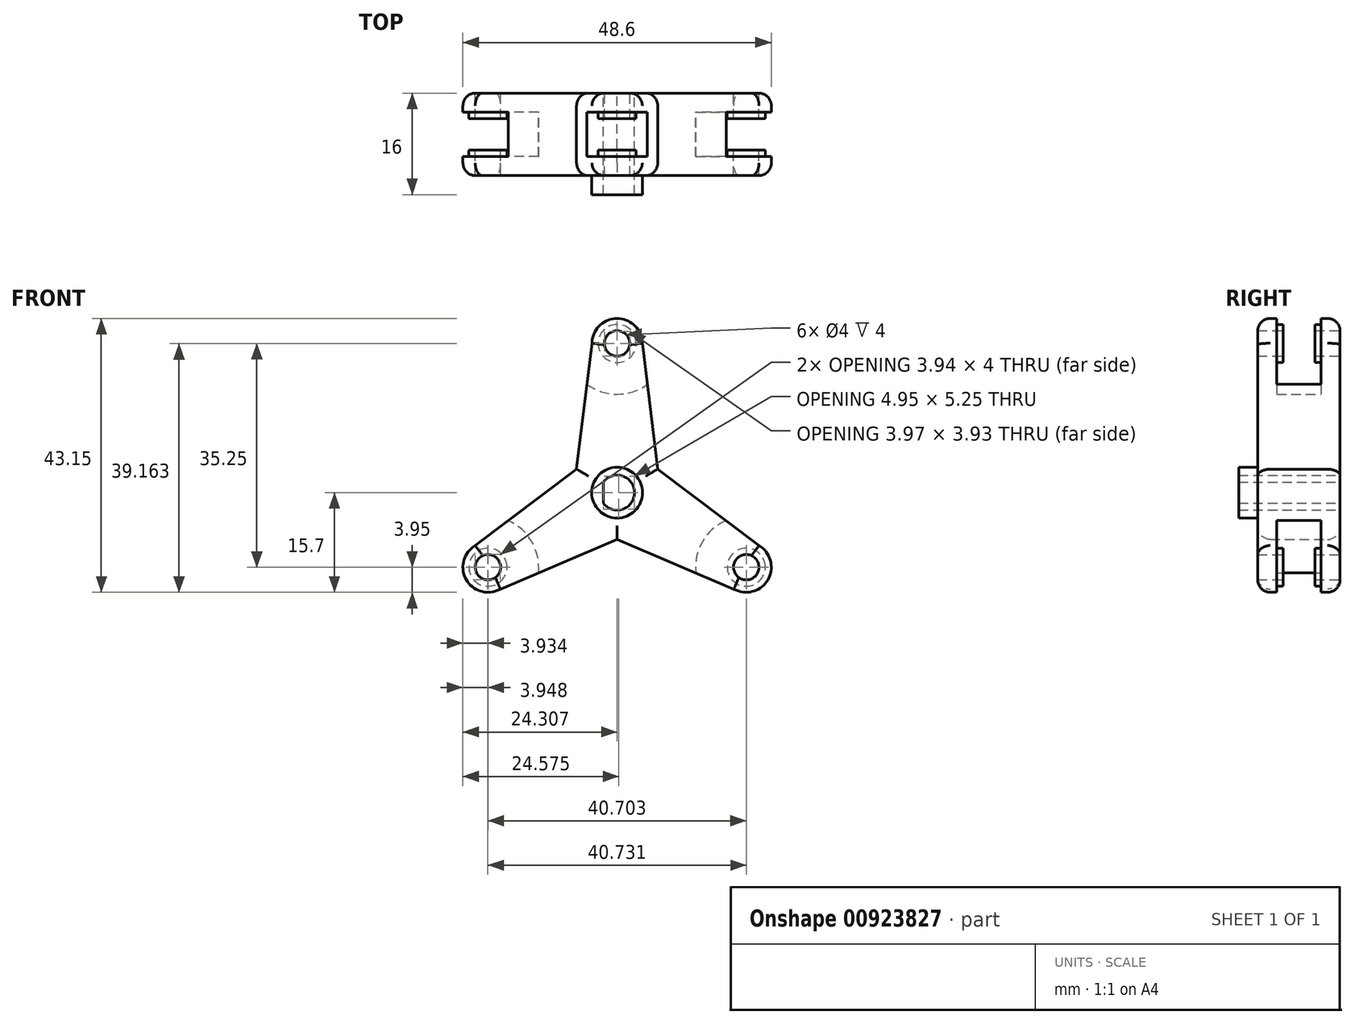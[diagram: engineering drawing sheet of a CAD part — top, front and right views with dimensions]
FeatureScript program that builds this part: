
annotation { "Feature Type Name" : "Feature", "Feature Type Description" : "" }
export const myFeature = defineFeature(function(context is Context, id is Id, definition is map)
    precondition{}
    {
        {
            var Q0;
            Q0=qCreatedBy(makeId("Front.planeOp"),FACE);
            var sketch = newSketch(context, id + "F0", { "sketchPlane" : qUnion([Q0])});
            skPoint(sketch, "E0", {"position": v(0, 23.5) * mm});
            skCircle(sketch, "E1", {"center": v(0, 23.5) * mm, "radius": 2 * mm});
            skPoint(sketch, "E2.center", {"position": v(0, 0) * mm});
            skArc(sketch, "E3", {"start": v(-2.2, -1.65) * mm, "mid": v(2.75, 0) * mm, "end": v(-2.2, 1.65) * mm});
            skCircle(sketch, "E4", {"center": v(0, 0) * mm, "radius": 4 * mm});
            skCircle(sketch, "E5", {"center": v(0, 23.5) * mm, "radius": 3 * mm});
            skArc(sketch, "E6", {"start": v(-4.76, 17.07) * mm, "mid": v(0, 15.5) * mm, "end": v(4.76, 17.07) * mm});
            skArc(sketch, "E7", {"start": v(3.92, 23.98) * mm, "mid": v(0, 27.45) * mm, "end": v(-3.92, 23.98) * mm});
            skLineSegment(sketch, "E8", {"start": v(-7.5, -5.33) * mm, "end": v(-3.92, 23.98) * mm});
            skLineSegment(sketch, "E9.MirrorCS", {"start": v(7.5, -5.33) * mm, "end": v(3.92, 23.98) * mm});
            skLineSegment(sketch, "E10", {"start": v(-2.2, 1.65) * mm, "end": v(-2.2, -1.65) * mm});
            skPoint(sketch, "E11.center", {"position": v(-0.14, 0.25) * mm});
            skArc(sketch, "E12.1.0", {"start": v(-22.73, -8.6) * mm, "mid": v(-23.77, -13.73) * mm, "end": v(-18.8, -15.39) * mm});
            skCircle(sketch, "E12.1.1", {"center": v(-20.35, -11.75) * mm, "radius": 2 * mm});
            skCircle(sketch, "E12.1.2", {"center": v(-20.35, -11.75) * mm, "radius": 3 * mm});
            skArc(sketch, "E12.1.3", {"start": v(-12.4, -12.66) * mm, "mid": v(-13.42, -7.75) * mm, "end": v(-17.17, -4.41) * mm});
            skPoint(sketch, "E12.1.4", {"position": v(-20.35, -11.75) * mm});
            skLineSegment(sketch, "E12.1.5", {"start": v(0.87, 9.16) * mm, "end": v(-22.73, -8.6) * mm});
            skLineSegment(sketch, "E12.1.6", {"start": v(8.37, -3.83) * mm, "end": v(-18.8, -15.39) * mm});
            skArc(sketch, "E12.2.0", {"start": v(18.8, -15.39) * mm, "mid": v(23.77, -13.73) * mm, "end": v(22.73, -8.6) * mm});
            skCircle(sketch, "E12.2.1", {"center": v(20.35, -11.75) * mm, "radius": 2 * mm});
            skCircle(sketch, "E12.2.2", {"center": v(20.35, -11.75) * mm, "radius": 3 * mm});
            skArc(sketch, "E12.2.3", {"start": v(17.17, -4.41) * mm, "mid": v(13.42, -7.75) * mm, "end": v(12.4, -12.66) * mm});
            skPoint(sketch, "E12.2.4", {"position": v(20.35, -11.75) * mm});
            skLineSegment(sketch, "E12.2.5", {"start": v(-8.37, -3.83) * mm, "end": v(18.8, -15.39) * mm});
            skLineSegment(sketch, "E12.2.6", {"start": v(-0.87, 9.16) * mm, "end": v(22.73, -8.6) * mm});
            skPoint(sketch, "E13", {"position": v(0, 27.45) * mm});
            skSolve(sketch);
        }
        {
            var Q0;
            Q0=makeQuery(id+"F0.imprint","IMPRINT",FACE,{"disambiguationData":[TD([[makeQuery(id+"F0.imprint","IMPRINT",EDGE,{"derivedFrom":sQuery(id+"F0.wireOp",EDGE,"E1")}),-1.0]])]});
            var Q1;
            Q1=makeQuery(id+"F0.imprint","IMPRINT",FACE,{"disambiguationData":[TD([[makeQuery(id+"F0.imprint","IMPRINT",EDGE,{"derivedFrom":sQuery(id+"F0.wireOp",EDGE,"E5")}),-1.0]])]});
            var Q2;
            {var subQ1=sQuery(id+"F0.wireOp",EDGE,"E6");Q2=makeQuery(id+"F0.imprint","IMPRINT",FACE,{"disambiguationData":[TD([[makeQuery(id+"F0.imprint","IMPRINT",EDGE,{"derivedFrom":subQ1}),-1.0]])]});}
            var Q3;
            {var subQ1=sQuery(id+"F0.wireOp",EDGE,"E12.2.3");Q3=makeQuery(id+"F0.imprint","IMPRINT",FACE,{"disambiguationData":[TD([[makeQuery(id+"F0.imprint","IMPRINT",EDGE,{"derivedFrom":subQ1}),-1.0]])]});}
            var Q4;
            {var subQ1=sQuery(id+"F0.wireOp",EDGE,"E12.2.0");Q4=makeQuery(id+"F0.imprint","IMPRINT",FACE,{"disambiguationData":[TD([[makeQuery(id+"F0.imprint","IMPRINT",EDGE,{"derivedFrom":subQ1}),1.0]])]});}
            var Q5;
            Q5=makeQuery(id+"F0.imprint","IMPRINT",FACE,{"disambiguationData":[TD([[makeQuery(id+"F0.imprint","IMPRINT",EDGE,{"derivedFrom":sQuery(id+"F0.wireOp",EDGE,"E12.2.1")}),-1.0]])]});
            var Q6;
            {var subQ1=sQuery(id+"F0.wireOp",EDGE,"E12.1.3");Q6=makeQuery(id+"F0.imprint","IMPRINT",FACE,{"disambiguationData":[TD([[makeQuery(id+"F0.imprint","IMPRINT",EDGE,{"derivedFrom":subQ1}),-1.0]])]});}
            var Q7;
            {var subQ1=sQuery(id+"F0.wireOp",EDGE,"E12.1.0");Q7=makeQuery(id+"F0.imprint","IMPRINT",FACE,{"disambiguationData":[TD([[makeQuery(id+"F0.imprint","IMPRINT",EDGE,{"derivedFrom":subQ1}),1.0]])]});}
            var Q8;
            Q8=makeQuery(id+"F0.imprint","IMPRINT",FACE,{"disambiguationData":[TD([[makeQuery(id+"F0.imprint","IMPRINT",EDGE,{"derivedFrom":sQuery(id+"F0.wireOp",EDGE,"E12.1.1")}),-1.0]])]});
            var Q9;
            Q9=makeQuery(id+"F0.imprint","IMPRINT",FACE,{"disambiguationData":[TD([[makeQuery(id+"F0.imprint","IMPRINT",EDGE,{"derivedFrom":sQuery(id+"F0.wireOp",EDGE,"E4")}),-1.0]])]});
            extrude(context, id + "F1", {"entities" : qUnion([Q0, Q1, Q2, Q3, Q4, Q5, Q6, Q7, Q8, Q9]), "depth" : 13 * mm, "offsetDistance" : 25 * mm});
        }
        {
            var Q0;
            Q0=makeQuery(id+"F0.imprint","IMPRINT",FACE,{"disambiguationData":[TD([[makeQuery(id+"F0.imprint","IMPRINT",EDGE,{"derivedFrom":sQuery(id+"F0.wireOp",EDGE,"E3")}),-1.0]])]});
            extrude(context, id + "F2", {"entities" : qUnion([Q0]), "operationType" : NewBodyOperationType.ADD, "depth" : 16 * mm, "offsetDistance" : 25 * mm});
        }
        {
            var Q0;
            Q0=makeQuery(id+"F0.imprint","IMPRINT",FACE,{"disambiguationData":[TD([[makeQuery(id+"F0.imprint","IMPRINT",EDGE,{"derivedFrom":sQuery(id+"F0.wireOp",EDGE,"E5")}),-1.0]])]});
            var Q1;
            {var subQ1=sQuery(id+"F0.wireOp",EDGE,"E12.1.0");Q1=makeQuery(id+"F0.imprint","IMPRINT",FACE,{"disambiguationData":[TD([[makeQuery(id+"F0.imprint","IMPRINT",EDGE,{"derivedFrom":subQ1}),1.0]])]});}
            var Q2;
            {var subQ1=sQuery(id+"F0.wireOp",EDGE,"E12.2.0");Q2=makeQuery(id+"F0.imprint","IMPRINT",FACE,{"disambiguationData":[TD([[makeQuery(id+"F0.imprint","IMPRINT",EDGE,{"derivedFrom":subQ1}),1.0]])]});}
            extrude(context, id + "F3", {"entities" : qUnion([Q0, Q1, Q2]), "operationType" : NewBodyOperationType.REMOVE, "endBound" : BoundingType.UP_TO_NEXT, "depth" : 25 * mm, "hasOffset" : true, "offsetDistance" : 3 * mm, "hasSecondDirection" : true, "secondDirectionOppositeDirection" : false, "secondDirectionDepth" : 3 * mm});
        }
        {
            var Q0;
            Q0=makeQuery(id+"F0.imprint","IMPRINT",FACE,{"disambiguationData":[TD([[makeQuery(id+"F0.imprint","IMPRINT",EDGE,{"derivedFrom":sQuery(id+"F0.wireOp",EDGE,"E1")}),-1.0]])]});
            var Q1;
            Q1=makeQuery(id+"F0.imprint","IMPRINT",FACE,{"disambiguationData":[TD([[makeQuery(id+"F0.imprint","IMPRINT",EDGE,{"derivedFrom":sQuery(id+"F0.wireOp",EDGE,"E12.1.1")}),-1.0]])]});
            var Q2;
            Q2=makeQuery(id+"F0.imprint","IMPRINT",FACE,{"disambiguationData":[TD([[makeQuery(id+"F0.imprint","IMPRINT",EDGE,{"derivedFrom":sQuery(id+"F0.wireOp",EDGE,"E12.2.1")}),-1.0]])]});
            extrude(context, id + "F4", {"entities" : qUnion([Q0, Q1, Q2]), "operationType" : NewBodyOperationType.REMOVE, "endBound" : BoundingType.UP_TO_NEXT, "depth" : 25 * mm, "hasOffset" : true, "offsetDistance" : 4 * mm, "hasSecondDirection" : true, "secondDirectionOppositeDirection" : false, "secondDirectionDepth" : 4 * mm});
        }
        {
            var Q0;
            Q0=makeQuery(id+"F1.opExtrude","CAP_EDGE",EDGE,{"disambiguationData":[OSD([sQuery(id+"F0.wireOp",EDGE,"E8")])],"isStart":false});
            var Q1;
            Q1=makeQuery(id+"F1.opExtrude","CAP_EDGE",EDGE,{"disambiguationData":[OSD([sQuery(id+"F0.wireOp",EDGE,"E12.2.6")])],"isStart":false});
            var Q2;
            Q2=makeQuery(id+"F1.opExtrude","CAP_EDGE",EDGE,{"disambiguationData":[OSD([sQuery(id+"F0.wireOp",EDGE,"E12.1.6")])],"isStart":false});
            var Q3;
            Q3=makeQuery(id+"F1.opExtrude","CAP_EDGE",EDGE,{"disambiguationData":[OSD([sQuery(id+"F0.wireOp",EDGE,"E9.MirrorCS")])],"isStart":true});
            var Q4;
            Q4=makeQuery(id+"F1.opExtrude","CAP_EDGE",EDGE,{"disambiguationData":[OSD([sQuery(id+"F0.wireOp",EDGE,"E12.1.5")])],"isStart":true});
            var Q5;
            Q5=makeQuery(id+"F1.opExtrude","CAP_EDGE",EDGE,{"disambiguationData":[OSD([sQuery(id+"F0.wireOp",EDGE,"E12.2.5")])],"isStart":true});
            var Q6;
            Q6=makeQuery(id+"F3.boolean.opBoolean","COPY",EDGE,{"derivedFrom":makeQuery(id+"F3.opExtrude","SWEPT_EDGE",EDGE,{"disambiguationData":[OSD([sQuery(id+"F0.wireOp",EDGE,"E6"),sQuery(id+"F0.wireOp",EDGE,"E9.MirrorCS")])]})});
            var Q7;
            Q7=makeQuery(id+"F3.boolean.opBoolean","COPY",EDGE,{"derivedFrom":makeQuery(id+"F3.opExtrude","SWEPT_EDGE",EDGE,{"disambiguationData":[OSD([sQuery(id+"F0.wireOp",EDGE,"E12.2.3"),sQuery(id+"F0.wireOp",EDGE,"E12.2.6")])]})});
            var Q8;
            Q8=makeQuery(id+"F3.boolean.opBoolean","COPY",EDGE,{"derivedFrom":makeQuery(id+"F3.opExtrude","SWEPT_EDGE",EDGE,{"disambiguationData":[OSD([sQuery(id+"F0.wireOp",EDGE,"E12.1.3"),sQuery(id+"F0.wireOp",EDGE,"E12.1.6")])]})});
            var Q9;
            Q9=makeQuery(id+"F3.boolean.opBoolean","COPY",EDGE,{"derivedFrom":makeQuery(id+"F3.opExtrude","SWEPT_EDGE",EDGE,{"disambiguationData":[OSD([sQuery(id+"F0.wireOp",EDGE,"E12.1.3"),sQuery(id+"F0.wireOp",EDGE,"E12.1.5")])]})});
            var Q10;
            Q10=makeQuery(id+"F3.boolean.opBoolean","COPY",EDGE,{"derivedFrom":makeQuery(id+"F3.opExtrude","SWEPT_EDGE",EDGE,{"disambiguationData":[OSD([sQuery(id+"F0.wireOp",EDGE,"E6"),sQuery(id+"F0.wireOp",EDGE,"E8")])]})});
            var Q11;
            Q11=makeQuery(id+"F3.boolean.opBoolean","COPY",EDGE,{"derivedFrom":makeQuery(id+"F3.opExtrude","SWEPT_EDGE",EDGE,{"disambiguationData":[OSD([sQuery(id+"F0.wireOp",EDGE,"E12.2.3"),sQuery(id+"F0.wireOp",EDGE,"E12.2.5")])]})});
            fillet(context, id + "F5", {"entities" : qUnion([Q0, Q1, Q2, Q3, Q4, Q5, Q6, Q7, Q8, Q9, Q10, Q11]), "radius" : 2 * mm, "tangentPropagation" : true, "allowEdgeOverflow" : false});
        }
    });
